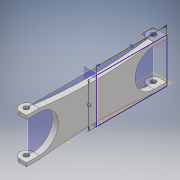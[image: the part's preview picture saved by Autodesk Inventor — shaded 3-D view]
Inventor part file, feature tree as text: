
AUTODESK INVENTOR PART (.ipt)
format: ipt  version: 2017 (Build 210142000, 142)  size: 438,272 bytes
history: native  units: mm
features: sketch x15, extrude x12, move_body x7, other x5, plane x4, direct_edit x3, projected_geometry x3, fillet x2, hole x2, mirror x1, reference x1
ambient origin geometry x8: Origin, YZ Plane, XZ Plane, XY Plane, X Axis, Y Axis, Z Axis, Center Point
bodies: Solid1 (feature_tree)
feature tree (55):
  plane  "Work Plane1"
  extrude  "Extrusion1"  Depth=7.0mm
  fillet  "Fillet1"  Radius=4.0mm
  plane  "Work Plane2"
  extrude  "Extrusion2"  Depth=52.0mm
  sketch  "Sketch3"  dims[d9=164.0mm d10=2.0mm d11=0.0mm]
  plane  "Work Plane3"
  mirror  "Mirror1"
  extrude  "Extrusion3"  Depth=2.0mm TaperAngle=0.0deg
  extrude  "Extrusion4"  Depth=4.0mm
  extrude  "Extrusion5"  Depth=12.0mm
  extrude  "Extrusion6"  Depth=1.0mm
  sketch  "Sketch8"  dims[d22=22.2mm d23=1.0mm]
  direct_edit  "Direct Edit1"
  extrude  "Extrusion7"  Depth=8.5mm
  extrude  "Extrusion8"  Depth=1.0mm
  extrude  "Extrusion9"  Depth=5.0mm
  extrude  "Extrusion10"  Depth=4.0mm
  direct_edit  "Direct Edit2"
  fillet  "Fillet3"  Radius=4.0mm
  hole  "Hole1"  [1 undecoded]
  plane  "Work Plane4"
  extrude  "Extrusion11"  Depth=1.0mm
  extrude  "Extrusion12"  Depth=22.0mm
  sketch  "Sketch14"  dims[d40=22.0mm d41=500.0mm]
  direct_edit  "Direct Edit3"
  hole  "Hole2"  [1 undecoded]
  sketch  "Sketch1"  dims[d2=4.0mm d3=0.0mm d4=7.0mm d5=4.0mm d6=0.0mm]
  reference  "Reference1"
  sketch  "Sketch2"  dims[d7=52.0mm d8=82.0mm]
  projected_geometry  "Projected Loop1"
  sketch  "Sketch4"  dims[d12=52.0mm d13=4.0mm]
  sketch  "Sketch5"  dims[d14=10.0mm d15=12.0mm]
  sketch  "Sketch6"  dims[d16=15.0mm d17=1.0mm]
  sketch  "Sketch7"  dims[d18=12.0mm d19=0.0mm d21=8.5mm]
  sketch  "Sketch9"  dims[d24=10.0mm d25=0.0mm d26=5.0mm]
  projected_geometry  "Projected Loop2"
  sketch  "Sketch10"  dims[d27=1.0mm d28=0.0mm d29=4.0mm d30=4.0mm]
  projected_geometry  "Projected Loop3"
  sketch  "Sketch11"  dims[d31=2.0mm d32=2.0mm]
  sketch  "Sketch12"  dims[d33=0.0mm d34=0.0mm d35=1.0mm d36=1.0mm]
  sketch  "Sketch13"  dims[d37=3.5mm d38=0.0mm d39=22.0mm]
  sketch  "Sketch15"  dims[d42=500.0mm d43=3.5mm d44=0.0mm d45=2.0mm d46=5.0mm d47=0.0mm d48=2.0mm d49=6.0mm d50=0.0mm d51=0.0mm d52=0.0mm d53=3.0mm d54=2.0mm d55=10.0mm d56=10.0mm d57=3.0mm d58=6.0mm d59=4.0mm d60=2.0mm d61=90.0deg d62=0.5mm d63=20.594885mm d64=1.0mm d68=6.0mm d69=0.0mm d70=6.0mm d71=0.0mm d72=0.0mm d73=0.0mm d74=-3.5mm d75=0.0mm d76=0.0mm d77=-0.25mm d78=0.0mm d79=0.0mm d80=-0.25mm d81=0.0mm d82=0.0mm d83=-0.25mm d84=0.0mm d85=0.0mm d86=-0.25mm d87=4.0mm d88=5.0mm d89=6.0mm d90=4.0mm d91=2.0mm d92=90.0deg d93=10.0mm d94=0.0mm]
  parser-record x1  (decoder bookkeeping rows leaked as tree rows — omitted from the tree; the rows remain in map.json)
  other  "assembly_full.iam"
  other  "top_right:1"
  move_body  "Move1"
  move_body  "Move2"
  move_body  "Move3"
  move_body  "Move4"
  move_body  "Move5"
  move_body  "Move6"
  move_body  "Move7"
  other  "Assembly4"
  other  "cap:1"
note: 2 required parameter values undecoded (feature->parameter linkage not recoverable at this tier; creation-order binding heuristic only, values carry confidence <= 0.55)
note: 1 file-system path scrubbed to <path> (originals preserved in map.json)
